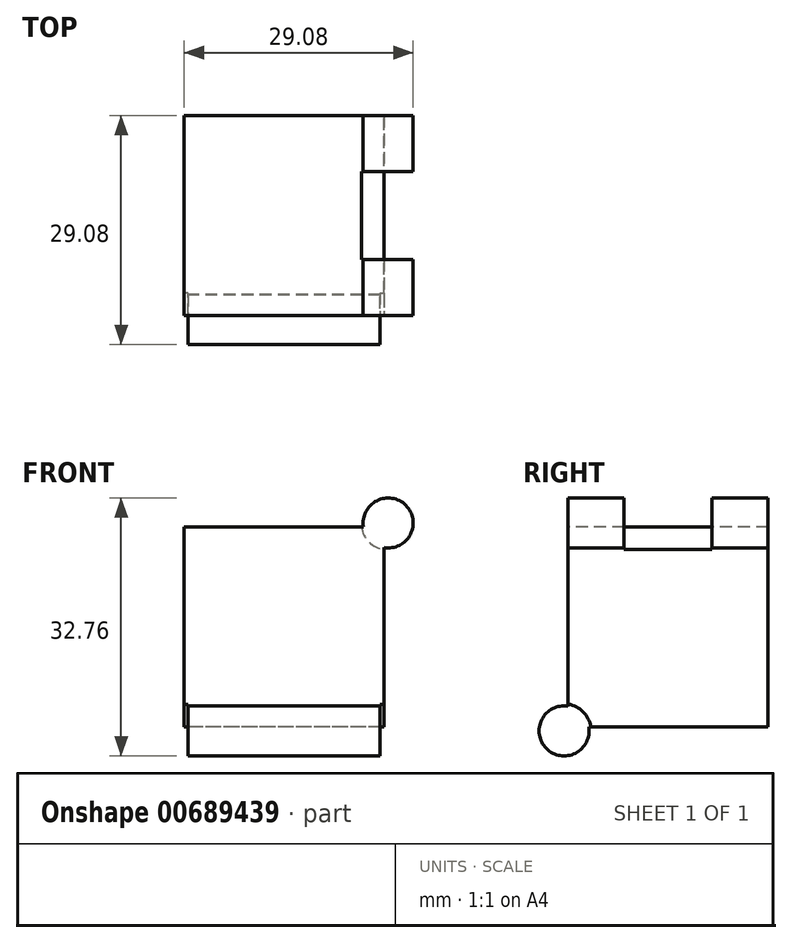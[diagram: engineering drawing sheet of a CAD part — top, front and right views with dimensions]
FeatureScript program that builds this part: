
annotation { "Feature Type Name" : "Feature", "Feature Type Description" : "" }
export const myFeature = defineFeature(function(context is Context, id is Id, definition is map)
    precondition{}
    {
        {
            assignVariable(context, id + "F0", {"name" : "O", "anyValue" : .2});
        }
        {
            var Q0;
            Q0=qCreatedBy(makeId("Front.planeOp"),FACE);
            var sketch = newSketch(context, id + "F1", { "sketchPlane" : qUnion([Q0])});
            skLineSegment(sketch, "E0.bottom", {"start": v(12.7, -12.7) * mm, "end": v(-12.7, -12.7) * mm});
            skLineSegment(sketch, "E0.top", {"start": v(12.7, 12.7) * mm, "end": v(-12.7, 12.7) * mm});
            skLineSegment(sketch, "E0.left", {"start": v(12.7, -12.7) * mm, "end": v(12.7, 12.7) * mm});
            skLineSegment(sketch, "E0.right", {"start": v(-12.7, -12.7) * mm, "end": v(-12.7, 12.7) * mm});
            skPoint(sketch, "E0.middle", {"position": v(0, 0) * mm});
            skSolve(sketch);
        }
        {
            var Q0;
            Q0=makeQuery(id+"F1.imprint","IMPRINT",FACE,{"disambiguationData":[TD([[makeQuery(id+"F1.imprint","IMPRINT",EDGE,{"derivedFrom":sQuery(id+"F1.wireOp",EDGE,"E0.bottom")}),-1.0]])]});
            extrude(context, id + "F2", {"entities" : qUnion([Q0]), "depth" : 25.4 * mm, "offsetDistance" : 25.4 * mm});
        }
        {
            var Q0;
            Q0=makeQuery(id+"F2.opExtrude","SWEPT_FACE",FACE,{"disambiguationData":[OSD([sQuery(id+"F1.wireOp",EDGE,"E0.right")])]});
            var sketch = newSketch(context, id + "F3", { "sketchPlane" : qUnion([Q0])});
            skCircle(sketch, "E1", {"center": v(25.9, -13.2) * mm, "radius": 3.18 * mm});
            skSolve(sketch);
        }
        {
            var Q0;
            {var subQ0=sQuery(id+"F3.wireOp",EDGE,"E1");var subQ1=sQuery(id+"F1.wireOp",EDGE,"E0.right");var subQ4=makeQuery(id+"F2.opExtrude","CAP_EDGE",EDGE,{"disambiguationData":[OSD([subQ1])],"isStart":false});var subQ5=makeQuery(id+"F3.imprint","INTERSECT",VERTEX,{"derivedFrom":[subQ4,subQ0]});Q0=makeQuery(id+"F3.imprint","IMPRINT",FACE,{"disambiguationData":[TD([[makeQuery(id+"F3.imprint","IMPRINT",EDGE,{"disambiguationData":[TD([[subQ5,1.0]])],"derivedFrom":subQ0}),1.0]])]});}
            var Q1;
            Q1=makeQuery(id+"F2.opExtrude","SWEPT_FACE",FACE,{"disambiguationData":[OSD([sQuery(id+"F1.wireOp",EDGE,"E0.left")])]});
            extrude(context, id + "F4", {"entities" : qUnion([Q0]), "operationType" : NewBodyOperationType.ADD, "endBound" : BoundingType.UP_TO_SURFACE, "oppositeDirection" : true, "depth" : 25.4 * mm, "endBoundEntityFace" : qUnion([Q1]), "offsetDistance" : 25.4 * mm});
        }
        {
            var Q0;
            {var subQ0=sQuery(id+"F1.wireOp",EDGE,"E0.left");Q0=makeQuery(id+"F4.boolean.opBoolean","MERGE",FACE,{"derivedFrom":[makeQuery(id+"F2.opExtrude","SWEPT_FACE",FACE,{"disambiguationData":[OSD([subQ0])]}),makeQuery(id+"F4.opExtrude","CAP_FACE",FACE,{"disambiguationData":[OSD([subQ0])],"isStart":false})]});}
            var sketch = newSketch(context, id + "F5", { "sketchPlane" : qUnion([Q0])});
            skCircle(sketch, "E2", {"center": v(-25.9, -13.2) * mm, "radius": 3.43 * mm});
            skSolve(sketch);
        }
        {
            var Q0;
            {var subQ0=sQuery(id+"F5.wireOp",EDGE,"E2");var subQ1=sQuery(id+"F1.wireOp",EDGE,"E0.left");var subQ5=makeQuery(id+"F2.opExtrude","CAP_EDGE",EDGE,{"disambiguationData":[OSD([subQ1])],"isStart":false});var subQ6=makeQuery(id+"F5.imprint","INTERSECT",VERTEX,{"derivedFrom":[subQ5,subQ0]});Q0=makeQuery(id+"F5.imprint","IMPRINT",FACE,{"disambiguationData":[TD([[makeQuery(id+"F5.imprint","IMPRINT",EDGE,{"disambiguationData":[TD([[subQ6,-1.0]])],"derivedFrom":subQ0}),1.0]])]});}
            var Q1;
            {var subQ0=sQuery(id+"F5.wireOp",EDGE,"E2");var subQ1=sQuery(id+"F1.wireOp",EDGE,"E0.left");var subQ5=makeQuery(id+"F2.opExtrude","CAP_EDGE",EDGE,{"disambiguationData":[OSD([subQ1])],"isStart":false});var subQ6=makeQuery(id+"F5.imprint","INTERSECT",VERTEX,{"derivedFrom":[subQ5,subQ0]});Q1=makeQuery(id+"F5.imprint","IMPRINT",FACE,{"disambiguationData":[TD([[makeQuery(id+"F5.imprint","IMPRINT",EDGE,{"disambiguationData":[TD([[subQ6,1.0]])],"derivedFrom":subQ0}),1.0]])]});}
            extrude(context, id + "F6", {"entities" : qUnion([Q0, Q1]), "operationType" : NewBodyOperationType.REMOVE, "oppositeDirection" : true, "depth" : (.3 + getVariable(context, 'O')) * mm, "offsetDistance" : 25.4 * mm});
        }
        {
            var Q0;
            {var subQ0=sQuery(id+"F1.wireOp",EDGE,"E0.right");Q0=makeQuery(id+"F4.boolean.opBoolean","MERGE",FACE,{"derivedFrom":[makeQuery(id+"F2.opExtrude","SWEPT_FACE",FACE,{"disambiguationData":[OSD([subQ0])]}),makeQuery(id+"F4.opExtrude","CAP_FACE",FACE,{"disambiguationData":[OSD([sQuery(id+"F1.wireOp",EDGE,"E0.bottom"),subQ0,sQuery(id+"F3.wireOp",EDGE,"E1")])],"isStart":true})]});}
            var sketch = newSketch(context, id + "F7", { "sketchPlane" : qUnion([Q0])});
            skCircle(sketch, "E3", {"center": v(25.9, -13.2) * mm, "radius": 3.43 * mm});
            skSolve(sketch);
        }
        {
            var Q0;
            {var subQ6=makeQuery(id+"F4.opExtrude","CAP_EDGE",EDGE,{"disambiguationData":[OSD([sQuery(id+"F3.wireOp",EDGE,"E1")])],"isStart":true});Q0=makeQuery(id+"F7.imprint","IMPRINT",FACE,{"disambiguationData":[TD([[makeQuery(id+"F7.imprint","IMPRINT",EDGE,{"derivedFrom":subQ6}),-1.0]])]});}
            var Q1;
            {var subQ6=makeQuery(id+"F4.opExtrude","CAP_EDGE",EDGE,{"disambiguationData":[OSD([sQuery(id+"F3.wireOp",EDGE,"E1")])],"isStart":true});Q1=makeQuery(id+"F7.imprint","IMPRINT",FACE,{"disambiguationData":[TD([[makeQuery(id+"F7.imprint","IMPRINT",EDGE,{"derivedFrom":subQ6}),1.0]])]});}
            extrude(context, id + "F8", {"entities" : qUnion([Q0, Q1]), "operationType" : NewBodyOperationType.REMOVE, "oppositeDirection" : true, "depth" : (.3 + getVariable(context, 'O')) * mm, "offsetDistance" : 25.4 * mm});
        }
        {
            var Q0;
            Q0=makeQuery(id+"F2.opExtrude","CAP_FACE",FACE,{"disambiguationData":[OSD([sQuery(id+"F1.wireOp",EDGE,"E0.bottom"),sQuery(id+"F1.wireOp",EDGE,"E0.top"),sQuery(id+"F1.wireOp",EDGE,"E0.left"),sQuery(id+"F1.wireOp",EDGE,"E0.right")])],"isStart":false});
            var sketch = newSketch(context, id + "F9", { "sketchPlane" : qUnion([Q0])});
            skCircle(sketch, "E4", {"center": v(13.2, 13.2) * mm, "radius": 3.18 * mm});
            skSolve(sketch);
        }
        {
            var Q0;
            {var subQ0=sQuery(id+"F9.wireOp",EDGE,"E4");var subQ1=makeQuery(id+"F2.opExtrude","CAP_EDGE",EDGE,{"disambiguationData":[OSD([sQuery(id+"F1.wireOp",EDGE,"E0.top")])],"isStart":false});var subQ2=makeQuery(id+"F9.imprint","INTERSECT",VERTEX,{"derivedFrom":[subQ1,subQ0]});Q0=makeQuery(id+"F9.imprint","IMPRINT",FACE,{"disambiguationData":[TD([[makeQuery(id+"F9.imprint","IMPRINT",EDGE,{"disambiguationData":[TD([[subQ2,1.0]])],"derivedFrom":subQ0}),1.0]])]});}
            var Q1;
            Q1=makeQuery(id+"F2.opExtrude","CAP_FACE",FACE,{"disambiguationData":[OSD([sQuery(id+"F1.wireOp",EDGE,"E0.bottom"),sQuery(id+"F1.wireOp",EDGE,"E0.top"),sQuery(id+"F1.wireOp",EDGE,"E0.left"),sQuery(id+"F1.wireOp",EDGE,"E0.right")])],"isStart":true});
            extrude(context, id + "F10", {"entities" : qUnion([Q0]), "operationType" : NewBodyOperationType.ADD, "endBound" : BoundingType.UP_TO_SURFACE, "oppositeDirection" : true, "depth" : 25.4 * mm, "endBoundEntityFace" : qUnion([Q1]), "offsetDistance" : 25.4 * mm});
        }
        {
            var Q0;
            {var subQ0=sQuery(id+"F1.wireOp",EDGE,"E0.left");Q0=makeQuery(id+"F4.boolean.opBoolean","MERGE",FACE,{"derivedFrom":[makeQuery(id+"F2.opExtrude","SWEPT_FACE",FACE,{"disambiguationData":[OSD([subQ0])]}),makeQuery(id+"F4.opExtrude","CAP_FACE",FACE,{"disambiguationData":[OSD([subQ0])],"isStart":false})]});}
            var sketch = newSketch(context, id + "F11", { "sketchPlane" : qUnion([Q0])});
            skLineSegment(sketch, "E5.bottom", {"start": v(-7.11, 4.13) * mm, "end": v(-18.29, 4.13) * mm});
            skLineSegment(sketch, "E5.top", {"start": v(-7.11, 21.77) * mm, "end": v(-18.29, 21.77) * mm});
            skLineSegment(sketch, "E5.left", {"start": v(-7.11, 4.13) * mm, "end": v(-7.11, 21.77) * mm});
            skLineSegment(sketch, "E5.right", {"start": v(-18.29, 4.13) * mm, "end": v(-18.29, 21.77) * mm});
            skPoint(sketch, "E5.middle", {"position": v(-12.7, 12.95) * mm});
            skSolve(sketch);
        }
        {
            var Q0;
            {var subQ0=sQuery(id+"F11.wireOp",EDGE,"E5.top");Q0=makeQuery(id+"F11.imprint","IMPRINT",FACE,{"disambiguationData":[TD([[makeQuery(id+"F11.imprint","IMPRINT",EDGE,{"derivedFrom":subQ0}),1.0]])]});}
            var Q1;
            {var subQ0=sQuery(id+"F11.wireOp",EDGE,"E5.bottom");Q1=makeQuery(id+"F11.imprint","IMPRINT",FACE,{"disambiguationData":[TD([[makeQuery(id+"F11.imprint","IMPRINT",EDGE,{"derivedFrom":subQ0}),-1.0]])]});}
            extrude(context, id + "F12", {"entities" : qUnion([Q0, Q1]), "operationType" : NewBodyOperationType.REMOVE, "depth" : 25.4 * mm, "offsetDistance" : 25.4 * mm});
        }
        {
            var Q0;
            Q0=makeQuery(id+"F12.boolean.opBoolean","COPY",FACE,{"derivedFrom":makeQuery(id+"F12.opExtrude","SWEPT_FACE",FACE,{"disambiguationData":[OSD([sQuery(id+"F11.wireOp",EDGE,"E5.left")])]})});
            var sketch = newSketch(context, id + "F13", { "sketchPlane" : qUnion([Q0])});
            skCircle(sketch, "E6", {"center": v(13.2, 13.2) * mm, "radius": 3.43 * mm});
            skSolve(sketch);
        }
        {
            var Q0;
            Q0=makeQuery(id+"F13.imprint","IMPRINT",FACE,{"disambiguationData":[TD([[makeQuery(id+"F13.imprint","IMPRINT",EDGE,{"derivedFrom":sQuery(id+"F13.wireOp",EDGE,"E6")}),1.0]])]});
            var Q1;
            Q1=makeQuery(id+"F12.boolean.opBoolean","COPY",FACE,{"derivedFrom":makeQuery(id+"F12.opExtrude","SWEPT_FACE",FACE,{"disambiguationData":[OSD([sQuery(id+"F11.wireOp",EDGE,"E5.right")])]})});
            extrude(context, id + "F14", {"entities" : qUnion([Q0]), "operationType" : NewBodyOperationType.REMOVE, "endBound" : BoundingType.UP_TO_SURFACE, "depth" : 25.4 * mm, "endBoundEntityFace" : qUnion([Q1]), "offsetDistance" : 25.4 * mm});
        }
    });
